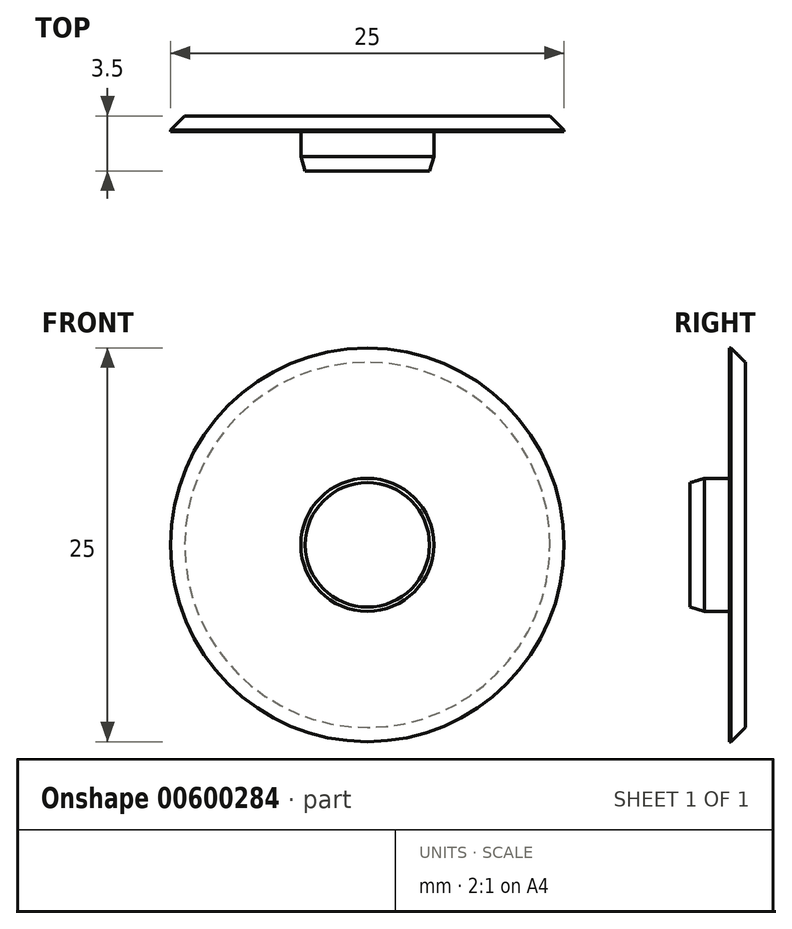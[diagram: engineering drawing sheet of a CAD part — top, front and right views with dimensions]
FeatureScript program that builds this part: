
annotation { "Feature Type Name" : "Feature", "Feature Type Description" : "" }
export const myFeature = defineFeature(function(context is Context, id is Id, definition is map)
    precondition{}
    {
        {
            var Q0;
            Q0=qCreatedBy(makeId("Right.planeOp"),FACE);
            var sketch = newSketch(context, id + "F0", { "sketchPlane" : qUnion([Q0])});
            skLineSegment(sketch, "E0", {"start": v(-0.63, 0) * mm, "end": v(3.5, 0) * mm, "construction": true});
            skLineSegment(sketch, "E1", {"start": v(3.5, 0) * mm, "end": v(3.5, 12.5) * mm});
            skLineSegment(sketch, "E2", {"start": v(2.5, 4.22) * mm, "end": v(2.5, 12.5) * mm});
            skLineSegment(sketch, "E3", {"start": v(2.5, 12.5) * mm, "end": v(3.5, 12.5) * mm});
            skLineSegment(sketch, "E4", {"start": v(3.5, 0) * mm, "end": v(0, 0) * mm});
            skLineSegment(sketch, "E5", {"start": v(0, 0) * mm, "end": v(0, 3.95) * mm});
            skLineSegment(sketch, "E6", {"start": v(0.9, 4.22) * mm, "end": v(2.5, 4.22) * mm});
            skLineSegment(sketch, "E7", {"start": v(0, 3.95) * mm, "end": v(0.9, 4.22) * mm});
            skSolve(sketch);
        }
        {
            var Q0;
            Q0=qSketchRegion(id+"F0",true);
            var Q1;
            Q1=sQuery(id+"F0.wireOp",EDGE,"E4");
            revolve(context, id + "F1", {"entities" : qUnion([Q0]), "axis" : qUnion([Q1]), "revolveType" : RevolveType.FULL});
        }
        {
            var Q0;
            Q0=makeQuery(id+"F1.opRevolve","SWEPT_EDGE",EDGE,{"disambiguationData":[OSD([sQuery(id+"F0.wireOp",EDGE,"E1"),sQuery(id+"F0.wireOp",EDGE,"E3")])]});
            chamfer(context, id + "F2", {"entities" : qUnion([Q0]), "width" : .9 * mm, "tangentPropagation" : true});
        }
    });
